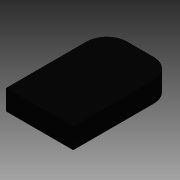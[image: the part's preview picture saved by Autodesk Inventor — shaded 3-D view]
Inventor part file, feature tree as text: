
AUTODESK INVENTOR PART (.ipt)
format: ipt  version: 2015 (Build 190159000, 159)  size: 76,288 bytes
history: native  units: in
note: dims shown in document units (in); Inventor stores cm internally (conversion verified against a paired STEP export)
features: extrude x1, sketch x1
ambient origin geometry x8: Origin, YZ Plane, XZ Plane, XY Plane, X Axis, Y Axis, Z Axis, Center Point
bodies: Solid1 (feature_tree)
feature tree (2):
  extrude  "Extrusion1"  Depth=1.65in
  sketch  "Sketch1"  dims[d0=2.475in d1=1.65in d2=0.5in d3=0.5in d4=0.0in]
